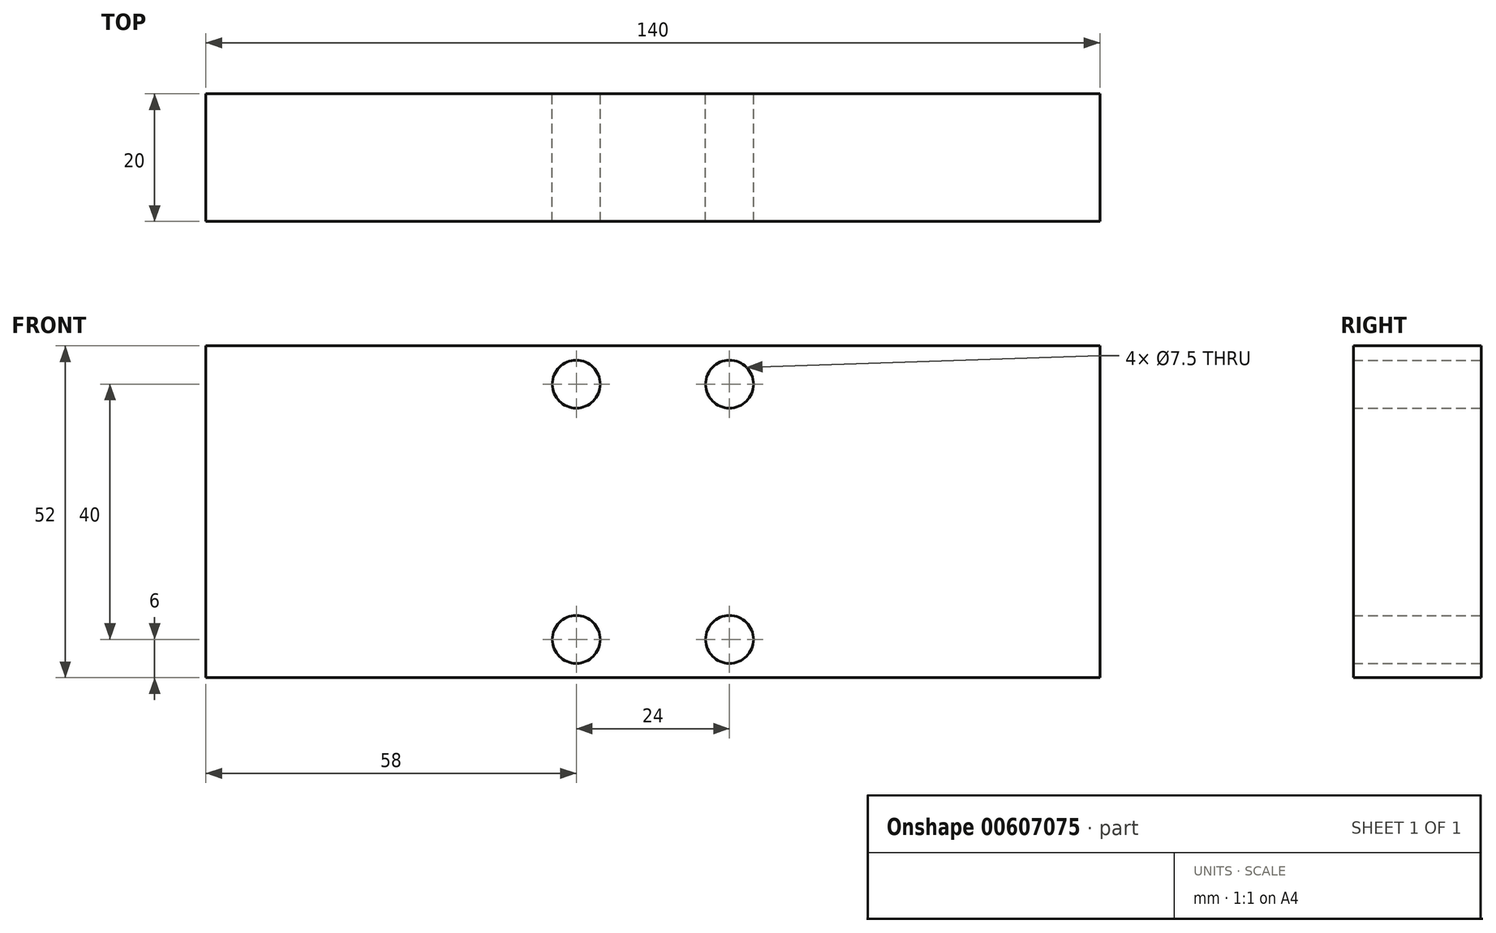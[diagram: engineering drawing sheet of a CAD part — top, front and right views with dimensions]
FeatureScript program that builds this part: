
annotation { "Feature Type Name" : "Feature", "Feature Type Description" : "" }
export const myFeature = defineFeature(function(context is Context, id is Id, definition is map)
    precondition{}
    {
        {
            var Q0;
            Q0=qCreatedBy(makeId("Front.planeOp"),FACE);
            var sketch = newSketch(context, id + "F0", { "sketchPlane" : qUnion([Q0]) });
            skLineSegment(sketch, "E0.bottom", {"start": v(20, 26) * mm, "end": v(-20, 26) * mm});
            skLineSegment(sketch, "E0.top", {"start": v(20, -26) * mm, "end": v(-20, -26) * mm});
            skLineSegment(sketch, "E0.left", {"start": v(20, 26) * mm, "end": v(20, -26) * mm});
            skLineSegment(sketch, "E0.right", {"start": v(-20, 26) * mm, "end": v(-20, -26) * mm});
            skPoint(sketch, "E0.middle", {"position": v(0, 0) * mm});
            skPoint(sketch, "E1", {"position": v(12, 20) * mm});
            skPoint(sketch, "E2", {"position": v(-12, 20) * mm});
            skPoint(sketch, "E3", {"position": v(12, -20) * mm});
            skPoint(sketch, "E4", {"position": v(-12, -20) * mm});
            skSolve(sketch);
        }
        {
            var Q0;
            Q0=makeQuery(id+"F0.imprint","IMPRINT",FACE,{"disambiguationData":[TD([[makeQuery(id+"F0.imprint","IMPRINT",EDGE,{"derivedFrom":sQuery(id+"F0.wireOp",EDGE,"E0.bottom")}),1.0]])]});
            extrude(context, id + "F1", {"entities" : qUnion([Q0]), "depth" : 20 * mm, "offsetDistance" : 25 * mm});
        }
        {
            var Q0;
            Q0=sQuery(id+"F0.wireOp",VERTEX,"E1");
            var Q1;
            Q1=sQuery(id+"F0.wireOp",VERTEX,"E2");
            var Q2;
            Q2=sQuery(id+"F0.wireOp",VERTEX,"E3");
            var Q3;
            Q3=sQuery(id+"F0.wireOp",VERTEX,"E4");
            var Q4;
            Q4=makeQuery(id+"F1.opExtrude","SWEPT_BODY",BODY,{"disambiguationData":[OSD([sQuery(id+"F0.wireOp",EDGE,"E0.bottom"),sQuery(id+"F0.wireOp",EDGE,"E0.top"),sQuery(id+"F0.wireOp",EDGE,"E0.left"),sQuery(id+"F0.wireOp",EDGE,"E0.right")])]});
            hole(context, id + "F2", {"style" : HoleStyle.SIMPLE, "endStyle" : HoleEndStyle.THROUGH, "oppositeDirection" : true, "holeDiameter" : 7.5 * mm, "majorDiameter" : 5 * mm, "isTappedThrough" : true, "tappedDepth" : 20 * mm, "tapClearance" : 0, "startFromSketch" : true, "locations" : qUnion([Q0, Q1, Q2, Q3]), "scope" : qUnion([Q4])});
        }
        {
            var Q0;
            Q0=makeQuery(id+"F1.opExtrude","SWEPT_FACE",FACE,{"disambiguationData":[OSD([sQuery(id+"F0.wireOp",EDGE,"E0.right")])]});
            var sketch = newSketch(context, id + "F3", { "sketchPlane" : qUnion([Q0]) });
            skLineSegment(sketch, "E5.0.0", {"start": v(0, 26) * mm, "end": v(0, -26) * mm});
            skLineSegment(sketch, "E5.0.1", {"start": v(0, -26) * mm, "end": v(20, -26) * mm});
            skLineSegment(sketch, "E5.0.2", {"start": v(20, -26) * mm, "end": v(20, 26) * mm});
            skLineSegment(sketch, "E5.0.3", {"start": v(20, 26) * mm, "end": v(0, 26) * mm});
            skSolve(sketch);
        }
        {
            var Q0;
            Q0=makeQuery(id+"F3.imprint","IMPRINT",FACE,{"disambiguationData":[TD([[makeQuery(id+"F3.imprint","IMPRINT",EDGE,{"derivedFrom":sQuery(id+"F3.wireOp",EDGE,"E5.0.0")}),1.0]])]});
            extrude(context, id + "F4", {"entities" : qUnion([Q0]), "operationType" : NewBodyOperationType.ADD, "depth" : 50 * mm, "offsetDistance" : 25 * mm});
        }
        {
            var Q0;
            Q0=makeQuery(id+"F1.opExtrude","SWEPT_FACE",FACE,{"disambiguationData":[OSD([sQuery(id+"F0.wireOp",EDGE,"E0.left")])]});
            var sketch = newSketch(context, id + "F5", { "sketchPlane" : qUnion([Q0]) });
            skLineSegment(sketch, "E6.0.0", {"start": v(0, -26) * mm, "end": v(0, 26) * mm});
            skLineSegment(sketch, "E6.0.1", {"start": v(0, 26) * mm, "end": v(-20, 26) * mm});
            skLineSegment(sketch, "E6.0.2", {"start": v(-20, 26) * mm, "end": v(-20, -26) * mm});
            skLineSegment(sketch, "E6.0.3", {"start": v(-20, -26) * mm, "end": v(0, -26) * mm});
            skSolve(sketch);
        }
        {
            var Q0;
            Q0=makeQuery(id+"F5.imprint","IMPRINT",FACE,{"disambiguationData":[TD([[makeQuery(id+"F5.imprint","IMPRINT",EDGE,{"derivedFrom":sQuery(id+"F5.wireOp",EDGE,"E6.0.0")}),-1.0]])]});
            extrude(context, id + "F6", {"entities" : qUnion([Q0]), "operationType" : NewBodyOperationType.ADD, "depth" : 50 * mm, "offsetDistance" : 25 * mm});
        }
    });
